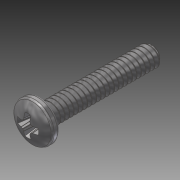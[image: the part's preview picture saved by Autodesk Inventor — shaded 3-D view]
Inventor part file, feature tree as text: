
AUTODESK INVENTOR PART (.ipt)
format: ipt  version: 2014 SP1 (Build 180222100, 222)  size: 812,032 bytes
history: native  units: in
note: dims shown in document units (in); Inventor stores cm internally (conversion verified against a paired STEP export)
features: fillet x1, other x1, imported_body x1
ambient origin geometry x8: Origin, YZ Plane, XZ Plane, XY Plane, X Axis, Y Axis, Z Axis, Center Point
bodies: Body1 (feature_tree)
feature tree (3):
  fillet  "Fillet1"  [1 undecoded]
  other  "91772A1121"
  imported_body  "Base1"
note: 1 required parameter value undecoded (feature->parameter linkage not recoverable at this tier; creation-order binding heuristic only, values carry confidence <= 0.55)
